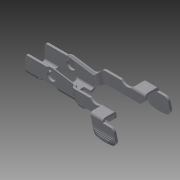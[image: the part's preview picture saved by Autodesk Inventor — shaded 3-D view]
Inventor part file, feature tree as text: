
AUTODESK INVENTOR PART (.ipt)
format: ipt  version: 2014 SP1 (Build 180222100, 222)  size: 860,672 bytes
history: native  units: in
note: dims shown in document units (in); Inventor stores cm internally (conversion verified against a paired STEP export)
features: projected_geometry x24, sketch x23, extrude x17, fillet x7, plane x7, reference x5, mirror x3, loft x2, revolve x1, chamfer x1, sweep x1, boolean_combine x1, other x1
ambient origin geometry x8: Origin, YZ Plane, XZ Plane, XY Plane, X Axis, Y Axis, Z Axis, Center Point
bodies: Solid1 (feature_tree), Solid2 (feature_tree)
feature tree (93):
  extrude  "Extrusion1"  Depth=0.474in
  extrude  "Extrusion2"  Depth=0.47in
  sketch  "Sketch3"  dims[d6=0.0965in d7=0.4765in d8=0.0in]
  fillet  "Fillet1"  Radius=0.377in
  fillet  "Fillet2"  Radius=0.061in
  extrude  "Extrusion3"  Depth=0.0965in TaperAngle=0.0deg
  plane  "Work Plane1"
  revolve  "Revolution1"  [1 undecoded]
  fillet  "Fillet3"  Radius=0.4765in
  chamfer  "Chamfer1"  Distance=0.4765in
  extrude  "Extrusion4"  Depth=0.245in
  sweep  "Sweep1"
  mirror  "Mirror1"
  sketch  "Sketch7"  dims[d15=0.0965in]
  plane  "Work Plane2"
  loft  "Loft1"
  extrude  "Extrusion5"  Depth=0.01in
  extrude  "Extrusion6"  Depth=0.01in
  extrude  "Extrusion7"  Depth=0.34in
  extrude  "Extrusion8"  Depth=0.724in
  fillet  "Fillet4"  Radius=0.0625in
  extrude  "Extrusion9"  [1 undecoded]
  extrude  "Extrusion10"  TaperAngle=0.0deg  [1 undecoded]
  fillet  "Fillet5"  Radius=0.06in
  plane  "Work Plane3"
  loft  "Loft2"
  extrude  "Extrusion11"  Depth=0.176in
  sketch  "Sketch20"  dims[d49=0.2405in d50=0.049in]
  extrude  "Extrusion12"  TaperAngle=45.0deg  [1 undecoded]
  extrude  "Extrusion13"  Depth=0.01in TaperAngle=0.0deg
  extrude  "Extrusion14"  Depth=0.01in
  mirror  "Mirror2"
  fillet  "Fillet6"  Radius=0.0462in
  extrude  "Extrusion15"  Depth=0.01in TaperAngle=0.0deg
  fillet  "Fillet7"  Radius=0.4765in
  plane  "Work Plane5"
  sketch  "Sketch22"  dims[d53=0.26in d54=45.0deg]
  plane  "Work Plane6"
  extrude  "Extrusion16"  Depth=0.01in TaperAngle=0.0deg
  plane  "Work Plane7"
  extrude  "Extrusion17"  Depth=0.01in
  mirror  "Mirror3"
  boolean_combine  "Combine1"
  sketch  "Sketch1"  dims[d0=0.057in d1=0.474in]
  reference  "Reference1"
  reference  "Reference2"
  reference  "Reference3"
  sketch  "Sketch2"  dims[d2=0.26in d3=0.47in d4=0.377in d5=0.061in]
  projected_geometry  "Projected Loop1"
  projected_geometry  "Projected Loop2"
  sketch  "Sketch4"  dims[d9=0.049in d10=0.049in d11=0.4765in d12=0.0in]
  projected_geometry  "Projected Loop3"
  other  "Work Axis1"
  sketch  "Sketch5"  dims[d13=0.0965in]
  sketch  "Sketch6"  dims[d14=0.0475in]
  projected_geometry  "Projected Loop4"
  projected_geometry  "Projected Loop5"
  sketch  "Sketch8"  dims[d16=0.0475in]
  projected_geometry  "Projected Loop6"
  sketch  "3D Sketch1"
  sketch  "Sketch9"  dims[d17=0.184in d18=0.4765in d19=0.0in]
  sketch  "Sketch10"  dims[d20=90.0deg d21=0.245in]
  reference  "Reference4"
  projected_geometry  "Projected Loop7"
  reference  "Reference5"
  sketch  "Sketch11"  dims[d22=0.1525in d23=0.1965in]
  projected_geometry  "Projected Loop8"
  projected_geometry  "Projected Loop9"
  projected_geometry  "Projected Loop10"
  projected_geometry  "Projected Loop11"
  sketch  "Sketch12"  dims[d24=0.1275in d25=0.069in]
  projected_geometry  "Projected Loop12"
  sketch  "Sketch13"  dims[d26=90.0deg d27=0.01in]
  sketch  "Sketch14"  dims[d28=0.01in d29=0.125in d30=45.0deg d31=0.1985in]
  projected_geometry  "Projected Loop13"
  sketch  "Sketch15"  dims[d32=0.235in d33=0.34in]
  projected_geometry  "Projected Loop14"
  sketch  "Sketch17"  dims[d34=0.4765in d35=0.0in d36=0.724in d39=0.0625in]
  projected_geometry  "Projected Loop16"
  sketch  "Sketch18"  dims[d40=0.0in d41=-0.137in]
  projected_geometry  "Projected Loop17"
  sketch  "Sketch19"  dims[d44=0.0in d45=90.0deg d46=0.0in d47=90.0deg d48=0.06in]
  projected_geometry  "Projected Loop18"
  plane  "Work Plane4"
  sketch  "Sketch21"  dims[d51=0.268in d52=0.176in]
  projected_geometry  "Projected Loop19"
  sketch  "Sketch23"  dims[d55=0.15in d56=0.4765in d57=0.0in d59=0.3375in d60=0.0462in d61=0.4765in d62=0.0in d63=0.4765in d64=0.0in d65=0.4765in d66=0.0in d67=0.0938in d68=0.049in d69=0.204in d70=0.0in d72=0.47in d73=0.0795in d74=0.049in d75=0.0in d76=0.335in d77=0.0938in d78=0.0335in d79=0.0475in d80=0.232in d81=0.1in d83=0.181in d84=0.0in d85=90.0deg d86=0.0in d87=90.0deg d88=0.049in d89=0.0in d90=0.049in d91=0.0in d92=0.049in d93=0.0in d94=0.049in d95=0.0in d96=0.04in d97=0.049in d98=0.0in d99=0.01in d100=-1.384in d101=0.049in d102=0.0695in d103=0.1455in d104=0.113in d109=1.271in d110=0.01in d111=0.348in d112=0.14in d114=0.01in d116=0.348in d117=0.1511in d118=0.1511in d119=0.14in d120=0.113in d121=0.0in d122=30.0deg d123=0.113in d124=0.0in]
  projected_geometry  "Project Cut Edges1"
  projected_geometry  "Project Cut Edges2"
  projected_geometry  "Project Cut Edges3"
  projected_geometry  "Project Cut Edges4"
  projected_geometry  "Project Cut Edges5"
  projected_geometry  "Project Cut Edges6"
note: 4 required parameter values undecoded (feature->parameter linkage not recoverable at this tier; creation-order binding heuristic only, values carry confidence <= 0.55)